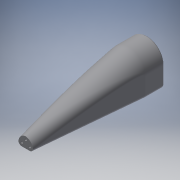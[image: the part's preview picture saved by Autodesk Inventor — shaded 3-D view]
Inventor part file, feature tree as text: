
AUTODESK INVENTOR PART (.ipt)
format: ipt  version: 2018 (Build 220112000, 112)  size: 365,568 bytes
history: native  units: in
note: dims shown in document units (in); Inventor stores cm internally (conversion verified against a paired STEP export)
features: extrude x11, sketch x11, fillet x7, reference x6, projected_geometry x3, other x2, plane x1
ambient origin geometry x8: Origin, YZ Plane, XZ Plane, XY Plane, X Axis, Y Axis, Z Axis, Center Point
bodies: Solid1 (feature_tree)
feature tree (41):
  extrude  "Extrusion1"  Depth=0.197in
  extrude  "Extrusion2"  Depth=0.15in
  extrude  "Extrusion3"  Depth=0.4in TaperAngle=0.0deg
  plane  "Work Plane1"
  extrude  "Extrusion13"  Depth=1.6in
  extrude  "Extrusion14"  Depth=0.0394in
  extrude  "Extrusion15"  Depth=0.098in
  fillet  "Fillet2"  Radius=0.098in
  fillet  "Fillet5"  Radius=0.5in
  fillet  "Fillet6"  Radius=0.6605in
  extrude  "Extrusion16"  Depth=0.25in
  extrude  "Extrusion17"  Depth=0.0787in
  fillet  "Fillet7"  Radius=0.0394in
  extrude  "Extrusion18"  Depth=5.9055in
  extrude  "Extrusion19"  Depth=1.0in TaperAngle=0.0deg
  fillet  "Fillet8"  Radius=100.0in
  fillet  "Fillet9"  Radius=0.8in
  fillet  "Fillet10"  Radius=1.1811in
  extrude  "Extrusion20"  Depth=0.3937in
  sketch  "Sketch1"  dims[d1=1.0in d2=0.0in d3=0.197in]
  reference  "Reference1"
  sketch  "Sketch2"  dims[d4=0.4in d5=0.0in d6=0.15in]
  reference  "Reference2"
  sketch  "Sketch3"  dims[d7=0.1772in d8=0.4in d9=0.0in]
  sketch  "Sketch14"  dims[d25=0.75in d26=1.6in]
  reference  "Reference5"
  reference  "Reference6"
  sketch  "Sketch15"  dims[d31=-0.8in d58=0.0394in]
  sketch  "Sketch16"  dims[d59=0.0394in d60=0.098in d61=0.098in d62=0.5in d63=0.0in d64=0.6605in d65=0.0in]
  sketch  "Sketch17"  dims[d66=0.25in d67=0.25in]
  sketch  "Sketch18"  dims[d68=0.6605in d69=0.0in d71=0.0787in d74=0.0394in]
  projected_geometry  "Projected Loop3"
  projected_geometry  "Projected Loop4"
  sketch  "Sketch19"  dims[d75=0.0394in d76=5.9055in]
  sketch  "Sketch20"  dims[d77=0.1969in d78=1.0in d79=0.0in d80=100.0in d81=0.0in d82=0.8in d83=1.1811in]
  projected_geometry  "Projected Loop5"
  sketch  "Sketch21"  dims[d84=100.0in d85=0.0in d86=0.3937in d87=0.3937in d88=100.0in d89=0.0in d90=0.4in d91=0.1575in d92=0.0787in d93=0.0984in d94=0.0984in d95=0.0984in d96=0.3543in d97=0.0in]
  reference  "Reference7"
  reference  "Reference8"
  other  "TailAssembly.iam"
  other  "Club1:1"
